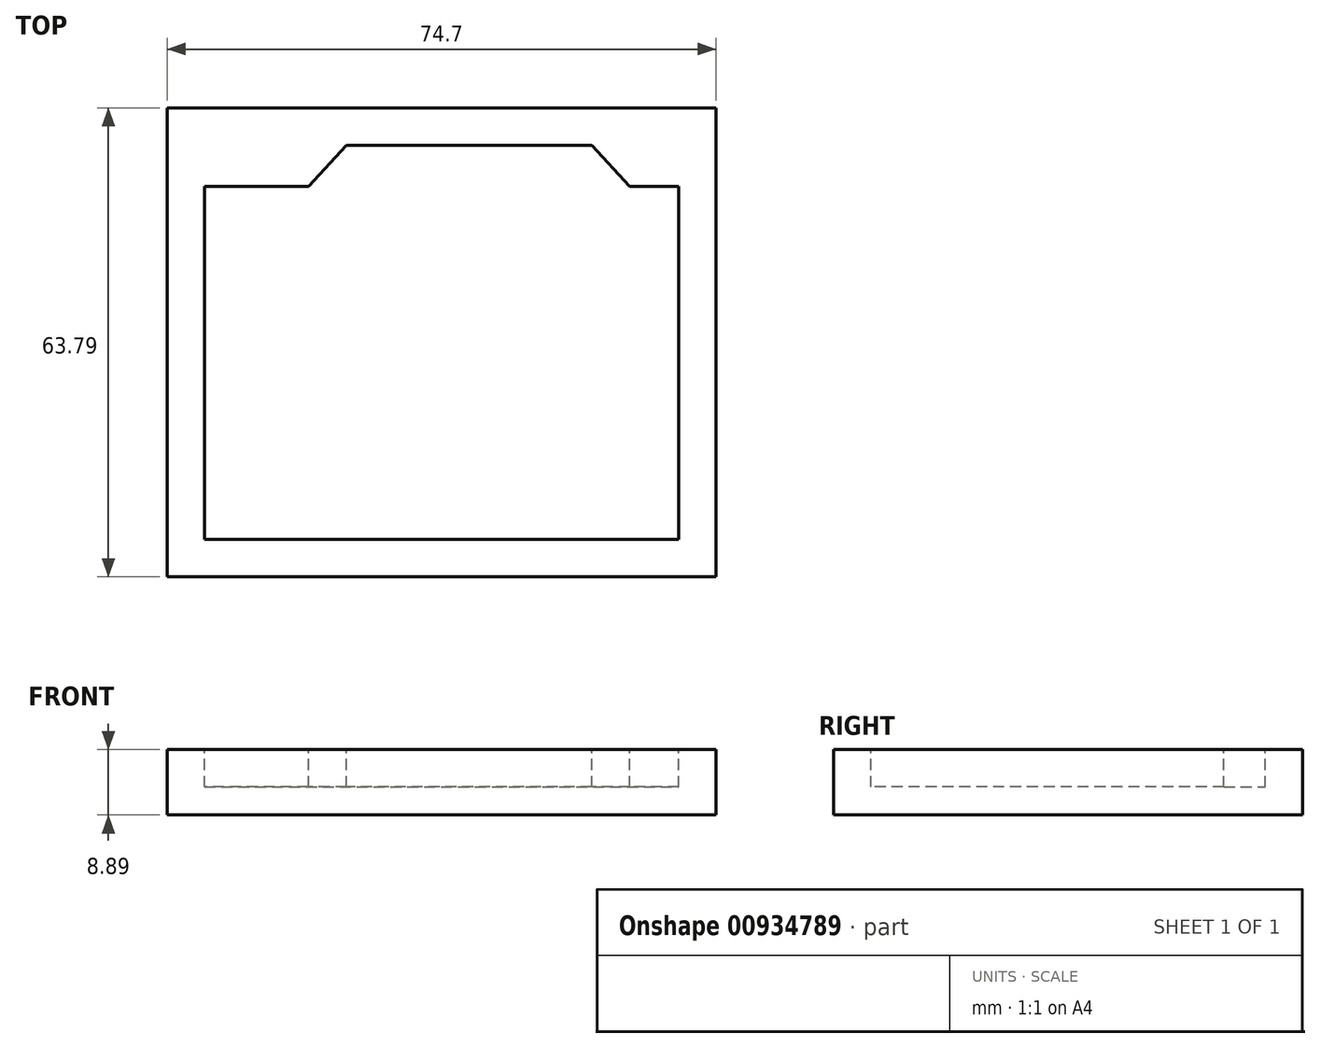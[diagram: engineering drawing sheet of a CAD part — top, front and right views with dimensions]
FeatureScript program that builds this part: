
annotation { "Feature Type Name" : "Feature", "Feature Type Description" : "" }
export const myFeature = defineFeature(function(context is Context, id is Id, definition is map)
    precondition{}
    {
        {
            var Q0;
            Q0=qCreatedBy(makeId("Top.planeOp"),FACE);
            var sketch = newSketch(context, id + "F0", { "sketchPlane" : qUnion([Q0])});
            skLineSegment(sketch, "E0", {"start": v(0, 0) * mm, "end": v(64.54, 0) * mm});
            skLineSegment(sketch, "E1", {"start": v(64.54, 0) * mm, "end": v(64.54, 48.02) * mm});
            skLineSegment(sketch, "E2", {"start": v(64.54, 48.02) * mm, "end": v(57.88, 48.02) * mm});
            skLineSegment(sketch, "E3", {"start": v(57.88, 48.02) * mm, "end": v(52.7, 53.63) * mm});
            skLineSegment(sketch, "E4", {"start": v(52.7, 53.63) * mm, "end": v(19.33, 53.63) * mm});
            skLineSegment(sketch, "E5", {"start": v(19.33, 53.63) * mm, "end": v(14.15, 48.02) * mm});
            skLineSegment(sketch, "E6", {"start": v(14.15, 48.02) * mm, "end": v(0, 48.02) * mm});
            skLineSegment(sketch, "E7", {"start": v(0, 48.02) * mm, "end": v(0, 0) * mm});
            skSolve(sketch);
        }
        {
            var Q0;
            Q0=qCreatedBy(makeId("Top.planeOp"),FACE);
            var sketch = newSketch(context, id + "F1", { "sketchPlane" : qUnion([Q0])});
            skLineSegment(sketch, "E8.bottom", {"start": v(69.62, 58.7) * mm, "end": v(-5.08, 58.7) * mm});
            skLineSegment(sketch, "E8.top", {"start": v(69.62, -5.08) * mm, "end": v(-5.08, -5.08) * mm});
            skLineSegment(sketch, "E8.left", {"start": v(69.62, 58.7) * mm, "end": v(69.62, -5.08) * mm});
            skLineSegment(sketch, "E8.right", {"start": v(-5.08, 58.7) * mm, "end": v(-5.08, -5.08) * mm});
            skPoint(sketch, "E8.middle", {"position": v(32.27, 26.81) * mm});
            skPoint(sketch, "E8.middle.positionSnap0", {"position": v(32.27, 0) * mm});
            skPoint(sketch, "E8.centerSnap0", {"position": v(32.27, 0) * mm});
            skSolve(sketch);
        }
        {
            var Q0;
            Q0 = qSketchRegion(id + "F1", true);
            extrude(context, id + "F2", {"entities" : qUnion([Q0]), "oppositeDirection" : true, "depth" : 8.9 * mm, "offsetDistance" : 25.4 * mm});
        }
        {
            var Q0;
            Q0 = qSketchRegion(id + "F0", true);
            extrude(context, id + "F3", {"entities" : qUnion([Q0]), "operationType" : NewBodyOperationType.REMOVE, "oppositeDirection" : true, "depth" : 5.08 * mm, "offsetDistance" : 25.4 * mm});
        }
    });
